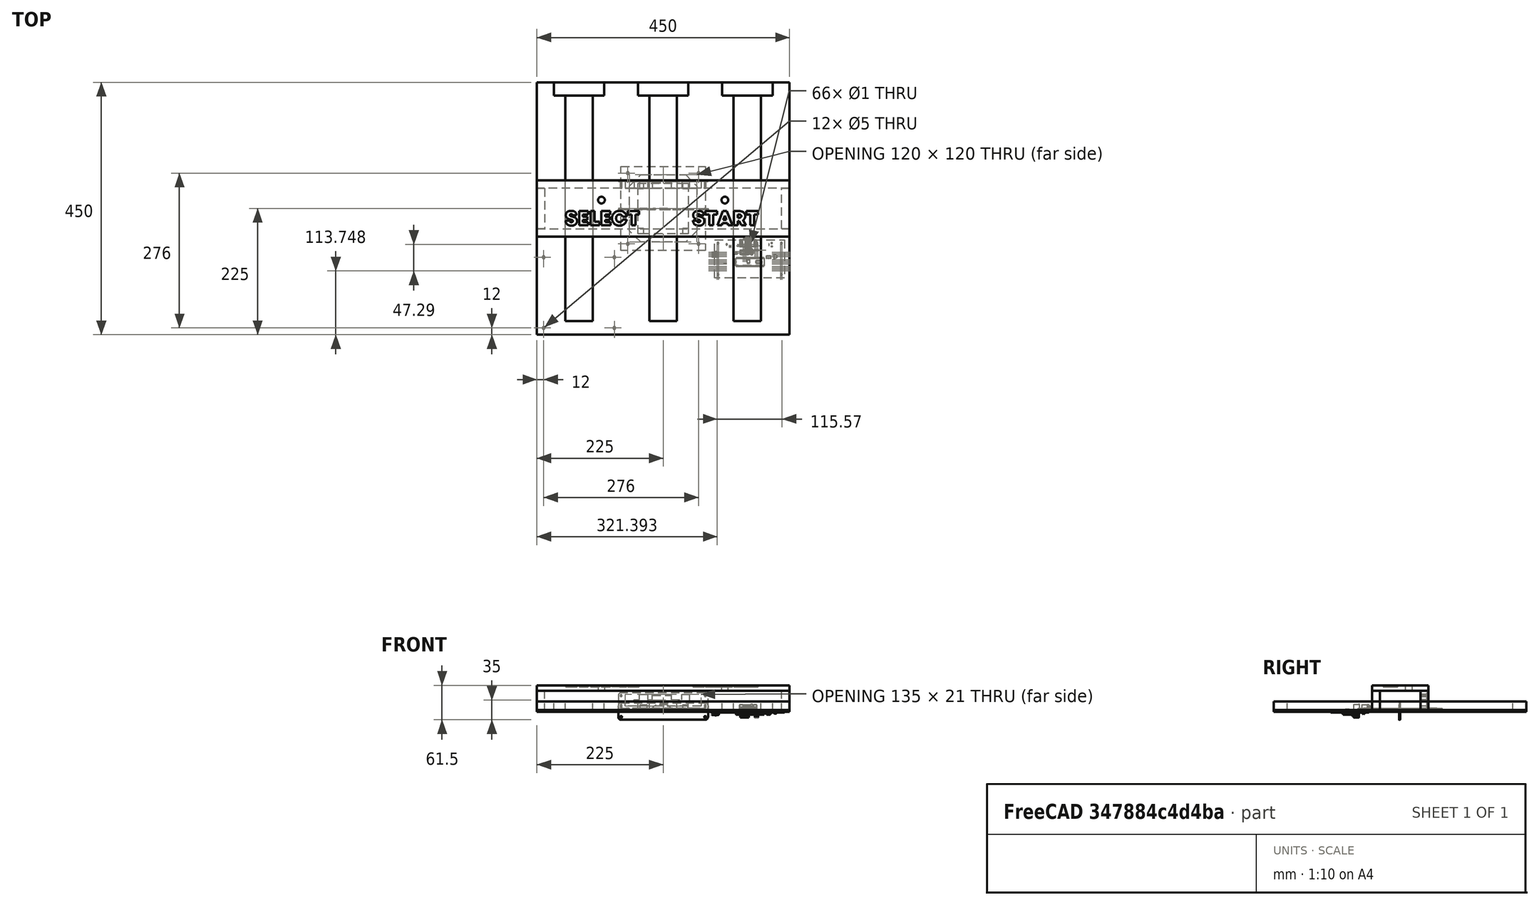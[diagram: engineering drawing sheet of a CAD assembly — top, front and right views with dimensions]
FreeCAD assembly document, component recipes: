
FREECAD ASSEMBLY — COMPONENT RECIPES ("LittleDancePad")

This assembly document has 13 components, labeled P0..P12 below (a component is one placed body or linked part). 12 of them carry a construction recipe — the FreeCAD feature program that regenerates the part from scratch, quoted from this document or its linked companion documents; the rest are supplied as boundary geometry only. No exploded tour is included for this assembly.
COMPONENT P0 — geometry summary ("PCB"; no construction recipe available for this part):
  bounding box: 135.6 x 74.1 x 23.8 mm
  tessellated surface: 47,226 triangles
  volume: 23545 mm^3 (10% of its bounding box)
COMPONENT P1 — recipe-attached ("Pad_BottomRight_Part", modeled in this document).
Construction recipe (the document's own serialized feature program — sketch geometry with constraints, then the solid features built on it; lengths are millimeters unless a unit is written):

FEATURE [Sketcher::SketchObject] Sketch001
  ArcFitTolerance = 0
  AttachmentSupport = -> [XY_Plane001]
  ExternalTypes = [0]
  FullyConstrained = true
  MakeInternals = false
  MapMode = 5
  _ExternalGeoVersion = 0
  sketch-geometry (4):
    g0: LineSegment StartX=-75 StartY=75 StartZ=0 EndX=75 EndY=75 EndZ=0
    g1: LineSegment StartX=75 StartY=75 StartZ=0 EndX=75 EndY=-75 EndZ=0
    g2: LineSegment StartX=75 StartY=-75 StartZ=0 EndX=-75 EndY=-75 EndZ=0
    g3: LineSegment StartX=-75 StartY=-75 StartZ=0 EndX=-75 EndY=75 EndZ=0
  constraints (11):
    c: Coincident(g0,g1)
    c: Coincident(g1,g2)
    c: Coincident(g2,g3)
    c: Coincident(g3,g0)
    c: Horizontal(g0)
    c: Horizontal(g2)
    c: Vertical(g1)
    c: Vertical(g3)
    c: Symmetric(g0,g1,g-1)
    c: DistanceX(g0,g0) = 150
    c: DistanceY(g1,g1) = 150
FEATURE [PartDesign::Pad] Pad001
  Direction = (0,0,1)
  Length = 6
  Length2 = 100
  Profile = -> Sketch001
  SideType = 0
  Suppressed = false
  Type = 0
  Type2 = 0
FEATURE [PartDesign::SubShapeBinder] Import  label="Import(*Sketch_Screw_Holes)"
  BindCopyOnChange = 0
  BindMode = 0
  ClaimChildren = false
  Context = -> Part [Body001.Import.]
  Fuse = false
  MakeFace = false
  OffsetFill = false
  OffsetIntersection = false
  OffsetJoinType = 0
  OffsetOpenResult = false
  PartialLoad = false
  Relative = true
  Support = -> [Link007]
  _Version = 8
FEATURE [PartDesign::Pocket] Pocket002
  BaseFeature = -> Pad001
  Direction = (0,0,-1)
  Length = 5
  Length2 = 100
  Profile = -> Import
  SideType = 2
  Suppressed = false
  Type = 1
  Type2 = 0
FEATURE [PartDesign::Body] Body001
  AllowCompound = true
  Group = -> [Sketch001,Pad001,Import,Pocket002]
  Origin = -> Origin006
  Tip = -> Pocket002
COMPONENT P2 — same part as P1; its construction recipe is shown at P1.
COMPONENT P3 — same part as P1; its construction recipe is shown at P1.
COMPONENT P4 — same part as P1; its construction recipe is shown at P1.
COMPONENT P5 — recipe-attached ("Pad_MiddleLeft_Part", modeled in this document).
Construction recipe (the document's own serialized feature program — sketch geometry with constraints, then the solid features built on it; lengths are millimeters unless a unit is written):

FEATURE [Sketcher::SketchObject] Sketch002
  ArcFitTolerance = 0
  AttachmentSupport = -> [XY_Plane002]
  ExternalTypes = [0]
  FullyConstrained = true
  MakeInternals = false
  MapMode = 5
  _ExternalGeoVersion = 0
  expr: Constraints[10] = <<Variables>>.PadLength
  expr: Constraints[9] = <<Variables>>.PadLength
  sketch-geometry (4):
    g0: LineSegment StartX=-75 StartY=75 StartZ=0 EndX=75 EndY=75 EndZ=0
    g1: LineSegment StartX=75 StartY=75 StartZ=0 EndX=75 EndY=-75 EndZ=0
    g2: LineSegment StartX=75 StartY=-75 StartZ=0 EndX=-75 EndY=-75 EndZ=0
    g3: LineSegment StartX=-75 StartY=-75 StartZ=0 EndX=-75 EndY=75 EndZ=0
  constraints (11):
    c: Coincident(g0,g1)
    c: Coincident(g1,g2)
    c: Coincident(g2,g3)
    c: Coincident(g3,g0)
    c: Horizontal(g0)
    c: Horizontal(g2)
    c: Vertical(g1)
    c: Vertical(g3)
    c: Symmetric(g0,g1,g-1)
    c: DistanceX(g0,g0) = 150
    c: DistanceY(g1,g1) = 150
FEATURE [PartDesign::Pad] Pad002
  Direction = (0,0,1)
  Length = 6
  Length2 = 100
  Profile = -> Sketch002
  SideType = 0
  Suppressed = false
  Type = 0
  Type2 = 0
  expr: Length = <<Variables>>.PadThickness
FEATURE [Sketcher::SketchObject] Sketch003
  ArcFitTolerance = 0
  AttachmentSupport = -> [XY_Plane002]
  ExternalGeometry = -> [Pad002]
  ExternalTypes = [0]
  FullyConstrained = true
  MakeInternals = false
  MapMode = 5
  _ExternalGeoVersion = 0
  expr: Constraints[10] = <<Variables>>.InnerPadBorderLength
  expr: Constraints[11] = <<Variables>>.InnerPadCornerLength
  expr: Constraints[12] = <<Variables>>.InnerPadBorderLength
  expr: Constraints[8] = <<Variables>>.InnerPadCornerLength
  sketch-geometry (8):
    g0: LineSegment StartX=-60 StartY=40 StartZ=0 EndX=-40 EndY=60 EndZ=0
    g1: LineSegment StartX=-40 StartY=60 StartZ=0 EndX=40 EndY=60 EndZ=0
    g2: LineSegment StartX=40 StartY=60 StartZ=0 EndX=60 EndY=40 EndZ=0
    g3: LineSegment StartX=60 StartY=40 StartZ=0 EndX=60 EndY=-40 EndZ=0
    g4: LineSegment StartX=60 StartY=-40 StartZ=0 EndX=40 EndY=-60 EndZ=0
    g5: LineSegment StartX=40 StartY=-60 StartZ=0 EndX=-40 EndY=-60 EndZ=0
    g6: LineSegment StartX=-40 StartY=-60 StartZ=0 EndX=-60 EndY=-40 EndZ=0
    g7: LineSegment StartX=-60 StartY=-40 StartZ=0 EndX=-60 EndY=40 EndZ=0
  constraints (18):
    c: Coincident(g0,g1)
    c: Coincident(g1,g2)
    c: Coincident(g2,g3)
    c: Coincident(g3,g4)
    c: Coincident(g4,g5)
    c: Coincident(g5,g6)
    c: Coincident(g6,g7)
    c: Coincident(g7,g0)
    c: DistanceX(g-3,g0) = 35
    c: Symmetric(g0,g1,g-2)
    c: DistanceY(g0,g-3) = 15
    c: DistanceY(g0,g-3) = 35
    c: DistanceX(g-3,g0) = 15
    c: Symmetric(g0,g6,g-1)
    c: Symmetric(g0,g5,g-1)
    c: Symmetric(g0,g2,g-2)
    c: Symmetric(g2,g3,g-1)
    c: Symmetric(g1,g4,g-1)
FEATURE [PartDesign::Pocket] Pocket
  BaseFeature = -> Pad002
  Direction = (0,0,-1)
  Length = 5
  Length2 = 100
  Profile = -> Sketch003
  SideType = 2
  Suppressed = false
  Type = 1
  Type2 = 0
FEATURE [Sketcher::SketchObject] Sketch004  label="Sketch_Screw_Holes"
  ArcFitTolerance = 0
  AttachmentSupport = -> [Pad002]
  ExternalGeometry = -> [Pad002]
  ExternalTypes = [0]
  FullyConstrained = true
  MakeInternals = false
  MapMode = 5
  Placement = pos=(0,0,0) rot=(1,0,0;3.14159rad)
  _ExternalGeoVersion = 0
  expr: Constraints[0] = <<Variables>>.ScrewCornerPosition
  expr: Constraints[1] = <<Variables>>.ScrewCornerPosition
  expr: Constraints[2] = <<Variables>>.PadScrewDiameter
  expr: Constraints[6] = <<Variables>>.PadScrewDiameter
  expr: Constraints[7] = <<Variables>>.PadScrewDiameter
  expr: Constraints[8] = <<Variables>>.PadScrewDiameter
  sketch-geometry (4):
    g0: Circle CenterX=-63 CenterY=63 CenterZ=0 NormalX=0 NormalY=0 NormalZ=1 AngleXU=0 Radius=2.5
    g1: Circle CenterX=63 CenterY=63 CenterZ=0 NormalX=0 NormalY=0 NormalZ=1 AngleXU=0 Radius=2.5
    g2: Circle CenterX=63 CenterY=-63 CenterZ=0 NormalX=0 NormalY=0 NormalZ=1 AngleXU=0 Radius=2.5
    g3: Circle CenterX=-63 CenterY=-63 CenterZ=0 NormalX=0 NormalY=0 NormalZ=1 AngleXU=0 Radius=2.5
  constraints (9):
    c: DistanceX(g-3,g0) = 12
    c: DistanceY(g0,g-3) = 12
    c: Diameter(g0) = 5
    c: Symmetric(g0,g1,g-2)
    c: Symmetric(g0,g3,g-1)
    c: Symmetric(g1,g2,g-1)
    c: Diameter(g1) = 5
    c: Diameter(g2) = 5
    c: Diameter(g3) = 5
FEATURE [PartDesign::Pocket] Pocket001  label="Screw_Pocket"
  BaseFeature = -> Pocket
  Direction = (0,0,1)
  Length = 5
  Length2 = 100
  Profile = -> Sketch004
  SideType = 2
  Suppressed = false
  Type = 1
  Type2 = 0
FEATURE [PartDesign::Body] Body002  label="Border_Body"
  AllowCompound = true
  Group = -> [Sketch002,Pad002,Sketch003,Sketch004,Pocket,Pocket001]
  Origin = -> Origin008
  Tip = -> Pocket001
FEATURE [Sketcher::SketchObject] Sketch005
  ArcFitTolerance = 0
  AttachmentSupport = -> [XY_Plane003]
  ExternalTypes = [0]
  FullyConstrained = true
  MakeInternals = false
  MapMode = 5
  _ExternalGeoVersion = 0
  expr: Constraints[9] = <<Variables>>.ContactLength
  sketch-geometry (4):
    g0: LineSegment StartX=-45 StartY=45 StartZ=0 EndX=45 EndY=45 EndZ=0
    g1: LineSegment StartX=45 StartY=45 StartZ=0 EndX=45 EndY=-45 EndZ=0
    g2: LineSegment StartX=45 StartY=-45 StartZ=0 EndX=-45 EndY=-45 EndZ=0
    g3: LineSegment StartX=-45 StartY=-45 StartZ=0 EndX=-45 EndY=45 EndZ=0
  constraints (11):
    c: Coincident(g0,g1)
    c: Coincident(g1,g2)
    c: Coincident(g2,g3)
    c: Coincident(g3,g0)
    c: Horizontal(g0)
    c: Horizontal(g2)
    c: Vertical(g1)
    c: Vertical(g3)
    c: Symmetric(g0,g1,g-1)
    c: DistanceX(g0,g0) = 90
    c: Equal(g0,g1)
FEATURE [PartDesign::Pad] Pad003
  Direction = (0,0,1)
  Length = 4
  Length2 = 100
  Profile = -> Sketch005
  SideType = 0
  Suppressed = false
  Type = 0
  Type2 = 0
FEATURE [PartDesign::Body] Body003  label="ContactBase_Body"
  AllowCompound = true
  Group = -> [Sketch005,Pad003]
  Origin = -> Origin010
  Tip = -> Pad003
COMPONENT P6 — same part as P5; its construction recipe is shown at P5.
COMPONENT P7 — same part as P5; its construction recipe is shown at P5.
COMPONENT P8 — recipe-attached ("Body_Part", modeled in this document).
Construction recipe (the document's own serialized feature program — sketch geometry with constraints, then the solid features built on it; lengths are millimeters unless a unit is written):

FEATURE [Sketcher::SketchObject] Sketch
  ArcFitTolerance = 0
  AttachmentSupport = -> [XY_Plane]
  ExternalTypes = [0]
  FullyConstrained = true
  MakeInternals = false
  MapMode = 5
  _ExternalGeoVersion = 0
  expr: Constraints[10] = <<Variables>>.OveralPadLength
  expr: Constraints[9] = <<Variables>>.OveralPadLength
  sketch-geometry (4):
    g0: LineSegment StartX=-225 StartY=225 StartZ=0 EndX=225 EndY=225 EndZ=0
    g1: LineSegment StartX=225 StartY=225 StartZ=0 EndX=225 EndY=-225 EndZ=0
    g2: LineSegment StartX=225 StartY=-225 StartZ=0 EndX=-225 EndY=-225 EndZ=0
    g3: LineSegment StartX=-225 StartY=-225 StartZ=0 EndX=-225 EndY=225 EndZ=0
  constraints (11):
    c: Coincident(g0,g1)
    c: Coincident(g1,g2)
    c: Coincident(g2,g3)
    c: Coincident(g3,g0)
    c: Horizontal(g0)
    c: Horizontal(g2)
    c: Vertical(g1)
    c: Vertical(g3)
    c: Symmetric(g0,g1,g-1)
    c: DistanceX(g0,g0) = 450
    c: DistanceY(g1,g1) = 450
FEATURE [PartDesign::Pad] Pad
  Direction = (0,0,1)
  Length = 18
  Length2 = 100
  Profile = -> Sketch
  SideType = 0
  Suppressed = false
  Type = 0
  Type2 = 0
  expr: Length = <<Variables>>.OverallPadThickness
FEATURE [PartDesign::Body] Body
  AllowCompound = true
  Group = -> [Sketch,Pad]
  Origin = -> Origin
  Tip = -> Pad
COMPONENT P9 — recipe-attached ("PolycarbonatePad_Part", modeled in this document).
Construction recipe (the document's own serialized feature program — sketch geometry with constraints, then the solid features built on it; lengths are millimeters unless a unit is written):

FEATURE [PartDesign::SubShapeBinder] Import003  label="Import003(*Sketch001)"
  BindCopyOnChange = 0
  BindMode = 0
  ClaimChildren = false
  Context = -> Part004 [Body006.Import003.]
  Fuse = false
  MakeFace = false
  OffsetFill = false
  OffsetIntersection = false
  OffsetJoinType = 0
  OffsetOpenResult = false
  PartialLoad = false
  Relative = true
  Support = -> [Link010]
  _Version = 8
FEATURE [PartDesign::Pad] Pad006
  Direction = (0,0,1)
  Length = 3
  Length2 = 100
  Profile = -> Import003
  SideType = 0
  Suppressed = false
  Type = 0
  Type2 = 0
FEATURE [PartDesign::SubShapeBinder] Import004  label="Import004(*Sketch_Screw_Holes)"
  BindCopyOnChange = 0
  BindMode = 0
  ClaimChildren = false
  Context = -> Part004 [Body006.Import004.]
  Fuse = false
  MakeFace = false
  OffsetFill = false
  OffsetIntersection = false
  OffsetJoinType = 0
  OffsetOpenResult = false
  PartialLoad = false
  Relative = true
  Support = -> [Link011]
  _Version = 8
FEATURE [PartDesign::Pocket] Pocket003
  BaseFeature = -> Pad006
  Direction = (0,0,-1)
  Length = 5
  Length2 = 100
  Profile = -> Import004
  SideType = 2
  Suppressed = false
  Type = 1
  Type2 = 0
FEATURE [PartDesign::LinearPattern] LinearPattern
  Direction = -> X_Axis007
  Length = 300
  Length2 = 100
  Mode = 0
  Mode2 = 0
  Occurrences = 3
  Occurrences2 = 1
  Offset = 150
  Offset2 = 10
  Reversed2 = false
  SpacingPattern = [0]
  SpacingPattern2 = [0]
  Spacings = [-1,-1]
  Suppressed = false
  TransformMode = 0
FEATURE [PartDesign::LinearPattern] LinearPattern001
  Direction = -> Y_Axis007
  Length = 300
  Length2 = 100
  Mode = 0
  Mode2 = 0
  Occurrences = 3
  Occurrences2 = 1
  Offset = 150
  Offset2 = 10
  Reversed2 = false
  SpacingPattern = [0]
  SpacingPattern2 = [0]
  Spacings = [-1,-1]
  Suppressed = false
  TransformMode = 0
FEATURE [PartDesign::MultiTransform] MultiTransform
  BaseFeature = -> Pocket003
  Originals = -> [Pocket003,Pad006]
  Suppressed = false
  TransformMode = 0
  Transformations = -> [LinearPattern,LinearPattern001]
FEATURE [PartDesign::Body] Body006
  AllowCompound = true
  Group = -> [Import003,Pad006,Import004,Pocket003,MultiTransform,LinearPattern,LinearPattern001]
  Origin = -> Origin014
  Tip = -> MultiTransform
COMPONENT P10 — recipe-attached ("Box_Part", modeled in this document).
Construction recipe (the document's own serialized feature program — sketch geometry with constraints, then the solid features built on it; lengths are millimeters unless a unit is written):

FEATURE [Sketcher::SketchObject] Sketch007
  ArcFitTolerance = 0
  AttachmentSupport = -> [XY_Plane008]
  ExternalTypes = [0]
  FullyConstrained = true
  MakeInternals = false
  MapMode = 5
  _ExternalGeoVersion = 0
  expr: Constraints[11] = <<Variables>>.OveralPadLength / 2
  expr: Constraints[8] = <<Variables>>.OveralPadLength
  sketch-geometry (4):
    g0: LineSegment StartX=-225 StartY=-36 StartZ=0 EndX=225 EndY=-36 EndZ=0
    g1: LineSegment StartX=225 StartY=-36 StartZ=0 EndX=225 EndY=-50 EndZ=0
    g2: LineSegment StartX=225 StartY=-50 StartZ=0 EndX=-225 EndY=-50 EndZ=0
    g3: LineSegment StartX=-225 StartY=-50 StartZ=0 EndX=-225 EndY=-36 EndZ=0
  constraints (12):
    c: Coincident(g0,g1)
    c: Coincident(g1,g2)
    c: Coincident(g2,g3)
    c: Coincident(g3,g0)
    c: Horizontal(g0)
    c: Horizontal(g2)
    c: Vertical(g1)
    c: Vertical(g3)
    c: DistanceX(g0,g0) = 450
    c: DistanceY(g3,g3) = 14
    c: DistanceY(g1,g-1) = 50
    c: DistanceX(g-1,g0) = 225
FEATURE [PartDesign::Pad] Pad007
  Direction = (0,0,1)
  Length = 37
  Length2 = 100
  Profile = -> Sketch007
  SideType = 0
  Suppressed = false
  Type = 0
  Type2 = 0
FEATURE [PartDesign::Body] Body007
  AllowCompound = true
  Group = -> [Sketch007,Pad007]
  Origin = -> Origin016
  Tip = -> Pad007
FEATURE [Sketcher::SketchObject] Sketch008
  ArcFitTolerance = 0
  AttachmentSupport = -> [XY_Plane009]
  ExternalTypes = [0]
  FullyConstrained = true
  MakeInternals = false
  MapMode = 5
  _ExternalGeoVersion = 0
  expr: Constraints[11] = <<Variables>>.OveralPadLength / 2
  expr: Constraints[8] = <<Variables>>.OveralPadLength
  sketch-geometry (4):
    g0: LineSegment StartX=-225 StartY=50 StartZ=0 EndX=225 EndY=50 EndZ=0
    g1: LineSegment StartX=225 StartY=50 StartZ=0 EndX=225 EndY=36 EndZ=0
    g2: LineSegment StartX=225 StartY=36 StartZ=0 EndX=-225 EndY=36 EndZ=0
    g3: LineSegment StartX=-225 StartY=36 StartZ=0 EndX=-225 EndY=50 EndZ=0
  constraints (12):
    c: Coincident(g0,g1)
    c: Coincident(g1,g2)
    c: Coincident(g2,g3)
    c: Coincident(g3,g0)
    c: Horizontal(g0)
    c: Horizontal(g2)
    c: Vertical(g1)
    c: Vertical(g3)
    c: DistanceX(g0,g0) = 450
    c: DistanceY(g1,g1) = 14
    c: DistanceY(g-1,g0) = 50
    c: DistanceX(g-1,g0) = 225
FEATURE [PartDesign::Pad] Pad008
  Direction = (0,0,1)
  Length = 37
  Length2 = 100
  Profile = -> Sketch008
  SideType = 0
  Suppressed = false
  Type = 0
  Type2 = 0
FEATURE [Sketcher::SketchObject] Sketch009
  ArcFitTolerance = 0
  AttachmentSupport = -> [XY_Plane010]
  ExternalTypes = [0]
  FullyConstrained = false
  MakeInternals = false
  MapMode = 5
  _ExternalGeoVersion = 0
  sketch-geometry (4):
    g0: LineSegment StartX=-225 StartY=36 StartZ=0 EndX=-211 EndY=36 EndZ=0
    g1: LineSegment StartX=-211 StartY=36 StartZ=0 EndX=-211 EndY=-36 EndZ=0
    g2: LineSegment StartX=-211 StartY=-36 StartZ=0 EndX=-225 EndY=-36 EndZ=0
    g3: LineSegment StartX=-225 StartY=-36 StartZ=0 EndX=-225 EndY=36 EndZ=0
  constraints (9):
    c: Coincident(g0,g1)
    c: Coincident(g1,g2)
    c: Coincident(g2,g3)
    c: Coincident(g3,g0)
    c: Horizontal(g0)
    c: Vertical(g1)
    c: Coincident(g0,g-3)
    c: Coincident(g2,g-4)
    c: DistanceX(g0,g0) = 14
FEATURE [PartDesign::Pad] Pad009
  Direction = (0,0,1)
  Length = 37
  Length2 = 100
  Profile = -> Sketch009
  SideType = 0
  Suppressed = false
  Type = 0
  Type2 = 0
FEATURE [PartDesign::Body] Body009
  AllowCompound = true
  Group = -> [Sketch009,Pad009]
  Origin = -> Origin018
  Tip = -> Pad009
FEATURE [Sketcher::SketchObject] Sketch010
  ArcFitTolerance = 0
  AttachmentSupport = -> [XY_Plane011]
  ExternalTypes = [0]
  FullyConstrained = true
  MakeInternals = false
  MapMode = 5
  _ExternalGeoVersion = 0
  sketch-geometry (4):
    g0: LineSegment StartX=211 StartY=36 StartZ=0 EndX=225 EndY=36 EndZ=0
    g1: LineSegment StartX=225 StartY=36 StartZ=0 EndX=225 EndY=-36 EndZ=0
    g2: LineSegment StartX=225 StartY=-36 StartZ=0 EndX=211 EndY=-36 EndZ=0
    g3: LineSegment StartX=211 StartY=-36 StartZ=0 EndX=211 EndY=36 EndZ=0
  constraints (10):
    c: Coincident(g0,g1)
    c: Coincident(g1,g2)
    c: Coincident(g2,g3)
    c: Coincident(g3,g0)
    c: Horizontal(g2)
    c: Vertical(g3)
    c: Coincident(g-3,g0)
    c: Coincident(g1,g-4)
    c: DistanceX(g0,g0) = 14
    c: Horizontal(g0)
FEATURE [PartDesign::Pad] Pad010
  Direction = (0,0,1)
  Length = 37
  Length2 = 100
  Profile = -> Sketch010
  SideType = 0
  Suppressed = false
  Type = 0
  Type2 = 0
FEATURE [PartDesign::Body] Body010
  AllowCompound = true
  Group = -> [Sketch010,Pad010]
  Origin = -> Origin019
  Tip = -> Pad010
FEATURE [Sketcher::SketchObject] Sketch011
  ArcFitTolerance = 0
  AttachmentSupport = -> [XY_Plane012]
  ExternalTypes = [0]
  FullyConstrained = true
  MakeInternals = false
  MapMode = 5
  _ExternalGeoVersion = 0
  sketch-geometry (4):
    g0: LineSegment StartX=-225 StartY=50 StartZ=0 EndX=225 EndY=50 EndZ=0
    g1: LineSegment StartX=225 StartY=50 StartZ=0 EndX=225 EndY=-50 EndZ=0
    g2: LineSegment StartX=225 StartY=-50 StartZ=0 EndX=-225 EndY=-50 EndZ=0
    g3: LineSegment StartX=-225 StartY=-50 StartZ=0 EndX=-225 EndY=50 EndZ=0
  constraints (9):
    c: Coincident(g0,g1)
    c: Coincident(g1,g2)
    c: Coincident(g2,g3)
    c: Coincident(g3,g0)
    c: Horizontal(g0)
    c: Vertical(g3)
    c: Coincident(g0,g-5)
    c: Coincident(g-6,g1)
    c: Coincident(g2,g-4)
FEATURE [PartDesign::Pad] Pad011
  Direction = (0,0,1)
  Length = 10
  Length2 = 100
  Profile = -> Sketch011
  SideType = 0
  Suppressed = false
  Type = 0
  Type2 = 0
FEATURE [Sketcher::SketchObject] Sketch012
  ArcFitTolerance = 0
  AttachmentSupport = -> [XY_Plane012]
  ExternalGeometry = -> [Pad011]
  ExternalTypes = [0]
  FullyConstrained = true
  MakeInternals = false
  MapMode = 5
  _ExternalGeoVersion = 0
  sketch-geometry (2):
    g0: Circle CenterX=110 CenterY=15 CenterZ=0 NormalX=0 NormalY=0 NormalZ=1 AngleXU=0 Radius=6
    g1: Circle CenterX=-110 CenterY=15 CenterZ=0 NormalX=0 NormalY=0 NormalZ=1 AngleXU=0 Radius=6
  constraints (5):
    c: Diameter(g0) = 12
    c: DistanceX(g-1,g0) = 110
    c: DistanceY(g0,g-3) = 35
    c: Diameter(g1) = 12
    c: Symmetric(g0,g1,g-2)
FEATURE [PartDesign::Pocket] Pocket004
  BaseFeature = -> Pad011
  Direction = (0,0,-1)
  Length = 5
  Length2 = 100
  Profile = -> Sketch012
  SideType = 2
  Suppressed = false
  Type = 1
  Type2 = 0
FEATURE [PartDesign::SubShapeBinder] Import011  label="Import011(START_ShapeString)"
  BindCopyOnChange = 0
  BindMode = 0
  ClaimChildren = false
  Context = -> Part005 [Body011.Import011.]
  Fuse = false
  MakeFace = false
  OffsetFill = false
  OffsetIntersection = false
  OffsetJoinType = 0
  OffsetOpenResult = false
  PartialLoad = false
  Relative = true
  Support = -> [ShapeString]
  _Version = 8
FEATURE [PartDesign::Pocket] Pocket005  label="START_Pocket"
  BaseFeature = -> Pocket004
  Direction = (0,0,-1)
  Length = 3.1
  Length2 = 100
  Profile = -> Import011
  SideType = 0
  Suppressed = false
  Type = 0
  Type2 = 0
FEATURE [PartDesign::SubShapeBinder] Import012  label="Import012(SELECT_ShapeString)"
  BindCopyOnChange = 0
  BindMode = 0
  ClaimChildren = false
  Context = -> Part005 [Body011.Pocket006.Import012.]
  Fuse = false
  MakeFace = false
  OffsetFill = false
  OffsetIntersection = false
  OffsetJoinType = 0
  OffsetOpenResult = false
  PartialLoad = false
  Relative = true
  Support = -> [ShapeString001]
  _Version = 8
FEATURE [PartDesign::Pocket] Pocket006  label="SELECT_Pocket"
  BaseFeature = -> Pocket005
  Direction = (0,0,-1)
  Length = 3.1
  Length2 = 100
  Profile = -> Import012
  SideType = 0
  Suppressed = false
  Type = 0
  Type2 = 0
FEATURE [PartDesign::Body] Body011  label="Panel_Body"
  AllowCompound = true
  Group = -> [Sketch011,Pad011,Sketch012,Pocket004,Import011,Pocket005,Import012,Pocket006]
  Origin = -> Origin020
  Placement = pos=(0,0,37) rot=(0,0,1;0rad)
  Tip = -> Pocket006
FEATURE [Sketcher::SketchObject] Sketch015
  ArcFitTolerance = 0
  AttachmentSupport = -> [Pad008]
  ExternalTypes = [0]
  FullyConstrained = true
  MakeInternals = false
  MapMode = 5
  Placement = pos=(0,50,0) rot=(0,0.707107,0.707107;3.14159rad)
  _ExternalGeoVersion = 0
  sketch-geometry (22):
    g0: LineSegment StartX=-67.5 StartY=18 StartZ=0 EndX=-46.5 EndY=18 EndZ=0
    g1: LineSegment StartX=-46.5 StartY=18 StartZ=0 EndX=-46.5 EndY=31 EndZ=0
    g2: LineSegment StartX=-46.5 StartY=31 StartZ=0 EndX=-33.5 EndY=31 EndZ=0
    g3: LineSegment StartX=-33.5 StartY=31 StartZ=0 EndX=-33.5 EndY=21 EndZ=0
    g4: LineSegment StartX=-33.5 StartY=21 StartZ=0 EndX=-14.5 EndY=21 EndZ=0
    g5: LineSegment StartX=-14.5 StartY=21 StartZ=0 EndX=-14.5 EndY=29 EndZ=0
    g6: LineSegment StartX=-14.5 StartY=29 StartZ=0 EndX=19.5 EndY=29 EndZ=0
    g7: LineSegment StartX=19.5 StartY=29 StartZ=0 EndX=19.5 EndY=21 EndZ=0
    g8: LineSegment StartX=19.5 StartY=21 StartZ=0 EndX=27.5 EndY=21 EndZ=0
    g9: LineSegment StartX=27.5 StartY=21 StartZ=0 EndX=27.5 EndY=31 EndZ=0
    g10: LineSegment StartX=27.5 StartY=31 StartZ=0 EndX=42.5 EndY=31 EndZ=0
    g11: LineSegment StartX=42.5 StartY=31 StartZ=0 EndX=42.5 EndY=21 EndZ=0
    g12: LineSegment StartX=67.5 StartY=18 StartZ=0 EndX=67.5 EndY=10 EndZ=0
    g13: LineSegment StartX=67.5 StartY=10 StartZ=0 EndX=-67.5 EndY=10 EndZ=0
    g14: LineSegment StartX=-67.5 StartY=10 StartZ=0 EndX=-67.5 EndY=18 EndZ=0
    g15: LineSegment StartX=42.5 StartY=21 StartZ=0 EndX=51.5 EndY=21 EndZ=0
    g16: LineSegment StartX=51.5 StartY=21 StartZ=0 EndX=51.5 EndY=18 EndZ=0
    g17: LineSegment StartX=51.5 StartY=18 StartZ=0 EndX=67.5 EndY=18 EndZ=0
    g18: Circle CenterX=-75 CenterY=28.5 CenterZ=0 NormalX=0 NormalY=0 NormalZ=1 AngleXU=0 Radius=1.75
    g19: Circle CenterX=-75 CenterY=8.5 CenterZ=0 NormalX=0 NormalY=0 NormalZ=1 AngleXU=0 Radius=1.75
    g20: Circle CenterX=75 CenterY=28.5 CenterZ=0 NormalX=0 NormalY=0 NormalZ=1 AngleXU=0 Radius=1.75
    g21: Circle CenterX=75 CenterY=8.5 CenterZ=0 NormalX=0 NormalY=0 NormalZ=1 AngleXU=0 Radius=1.75
  constraints (65):
    c: Horizontal(g0)
    c: Coincident(g0,g1)
    c: Vertical(g1)
    c: Coincident(g1,g2)
    c: Horizontal(g2)
    c: Coincident(g2,g3)
    c: Vertical(g3)
    c: Coincident(g3,g4)
    c: Horizontal(g4)
    c: Vertical(g5)
    c: Coincident(g5,g6)
    c: Horizontal(g6)
    c: Coincident(g6,g7)
    c: Vertical(g7)
    c: Coincident(g7,g8)
    c: Horizontal(g8)
    c: Coincident(g8,g9)
    c: Coincident(g9,g10)
    c: Horizontal(g10)
    c: Coincident(g10,g11)
    c: Vertical(g12)
    c: Coincident(g12,g13)
    c: Coincident(g13,g14)
    c: Coincident(g14,g0)
    c: Vertical(g14)
    c: DistanceX(g13,g13) = 135
    c: Symmetric(g13,g12,g-2)
    c: DistanceY(g14,g14) = 8
    c: DistanceY(g12,g12) = 8
    c: DistanceY(g-1,g0) = 18
    c: DistanceX(g0,g0) = 21
    c: DistanceX(g2,g2) = 13
    c: DistanceY(g1,g1) = 13
    c: DistanceY(g3,g3) = 10
    c: DistanceY(g7,g7) = 8
    c: DistanceY(g9,g9) = 10
    c: DistanceY(g11,g11) = 10
    c: Vertical(g9)
    c: Vertical(g11)
    c: Coincident(g11,g15)
    c: Horizontal(g15)
    c: Coincident(g15,g16)
    c: Vertical(g16)
    c: Coincident(g16,g17)
    c: Coincident(g17,g12)
    c: Horizontal(g17)
    c: Coincident(g5,g4)
    c: DistanceY(g5,g5) = 8
    c: DistanceX(g4,g4) = 19
    c: DistanceX(g6,g6) = 34
    c: DistanceX(g8,g8) = 8
    c: DistanceX(g10,g10) = 15
    c: DistanceX(g17,g17) = 16
    c: Diameter(g18) = 3.5
    c: Diameter(g19) = 3.5
    c: Diameter(g20) = 3.5
    c: Diameter(g21) = 3.5
    c: DistanceY(g-1,g19) = 8.5
    c: DistanceY(g-1,g21) = 8.5
    c: DistanceY(g-1,g18) = 28.5
    c: DistanceY(g-1,g20) = 28.5
    c: DistanceX(g19,g-1) = 75
    c: DistanceX(g18,g-1) = 75
    c: DistanceX(g-1,g21) = 75
    c: DistanceX(g-1,g20) = 75
FEATURE [PartDesign::Pocket] Pocket007
  BaseFeature = -> Pad008
  Direction = (0,-1,2e-16)
  Length = 5
  Length2 = 100
  Profile = -> Sketch015
  SideType = 2
  Suppressed = false
  Type = 1
  Type2 = 0
FEATURE [Sketcher::SketchObject] Sketch016
  ArcFitTolerance = 0
  AttachmentSupport = -> [Pocket007]
  ExternalGeometry = -> [Pocket007]
  ExternalTypes = [0]
  FullyConstrained = true
  MakeInternals = false
  MapMode = 5
  Placement = pos=(0,50,0) rot=(0,0.707107,0.707107;3.14159rad)
  _ExternalGeoVersion = 0
  sketch-geometry (4):
    g0: LineSegment StartX=-14.5 StartY=31 StartZ=0 EndX=19.5 EndY=31 EndZ=0
    g1: LineSegment StartX=19.5 StartY=31 StartZ=0 EndX=19.5 EndY=29 EndZ=0
    g2: LineSegment StartX=19.5 StartY=29 StartZ=0 EndX=-14.5 EndY=29 EndZ=0
    g3: LineSegment StartX=-14.5 StartY=29 StartZ=0 EndX=-14.5 EndY=31 EndZ=0
  constraints (10):
    c: Coincident(g0,g1)
    c: Coincident(g1,g2)
    c: Coincident(g2,g3)
    c: Coincident(g3,g0)
    c: Horizontal(g0)
    c: Vertical(g1)
    c: Vertical(g3)
    c: Coincident(g2,g-3)
    c: Coincident(g1,g-3)
    c: DistanceY(g3,g3) = 2
FEATURE [PartDesign::Pocket] Pocket008
  BaseFeature = -> Pocket007
  Direction = (0,-1,2e-16)
  Length = 4.5
  Length2 = 100
  Profile = -> Sketch016
  SideType = 0
  Suppressed = false
  Type = 0
  Type2 = 0
FEATURE [Sketcher::SketchObject] Sketch019
  ArcFitTolerance = 0
  AttachmentSupport = -> [Pocket008]
  ExternalGeometry = -> [Pocket008]
  ExternalTypes = [0]
  FullyConstrained = true
  MakeInternals = false
  MapMode = 5
  Placement = pos=(0,50,0) rot=(0,0.707107,0.707107;3.14159rad)
  _ExternalGeoVersion = 0
  sketch-geometry (8):
    g0: ArcOfCircle CenterX=-75 CenterY=28.5 CenterZ=0 NormalX=0 NormalY=0 NormalZ=1 AngleXU=0 Radius=5 StartAngle=1.5708 EndAngle=3.14159
    g1: ArcOfCircle CenterX=-75 CenterY=8.5 CenterZ=0 NormalX=0 NormalY=0 NormalZ=1 AngleXU=0 Radius=5 StartAngle=3.14159 EndAngle=4.71239
    g2: ArcOfCircle CenterX=75 CenterY=28.5 CenterZ=0 NormalX=0 NormalY=0 NormalZ=1 AngleXU=0 Radius=5 StartAngle=4.5489e-06 EndAngle=1.5708
    g3: ArcOfCircle CenterX=75 CenterY=8.5 CenterZ=0 NormalX=0 NormalY=0 NormalZ=1 AngleXU=0 Radius=5 StartAngle=4.71239 EndAngle=6.28319
    g4: LineSegment StartX=-75 StartY=33.5 StartZ=0 EndX=75 EndY=33.5 EndZ=0
    g5: LineSegment StartX=80 StartY=28.5 StartZ=0 EndX=80 EndY=8.5 EndZ=0
    g6: LineSegment StartX=75 StartY=3.5 StartZ=0 EndX=-75 EndY=3.5 EndZ=0
    g7: LineSegment StartX=-80 StartY=8.5 StartZ=0 EndX=-80 EndY=28.5 EndZ=0
  constraints (26):
    c: Coincident(g4,g0)
    c: Coincident(g4,g2)
    c: Coincident(g5,g2)
    c: Coincident(g5,g3)
    c: Vertical(g5)
    c: Coincident(g6,g3)
    c: Coincident(g6,g1)
    c: Horizontal(g6)
    c: Coincident(g7,g1)
    c: Coincident(g7,g0)
    c: Vertical(g7)
    c: Radius(g0) = 5
    c: Radius(g1) = 5
    c: Radius(g2) = 5
    c: Radius(g3) = 5
    c: DistanceX(g1,g3) = 160
    c: DistanceY(g1,g0) = 30
    c: Symmetric(g0,g2,g-2)
    c: DistanceY(g-1,g1) = 3.5
    c: Symmetric(g1,g3,g-2)
    c: DistanceX(g1,g1) = 5
    c: DistanceX(g0,g0) = 5
    c: DistanceY(g0,g0) = 5
    c: DistanceY(g1,g1) = 5
    c: DistanceY(g3,g3) = 5
    c: DistanceX(g2,g2) = 5
FEATURE [PartDesign::Pocket] Pocket010
  BaseFeature = -> Pocket008
  Direction = (0,-1,2e-16)
  Length = 2
  Length2 = 100
  Profile = -> Sketch019
  SideType = 0
  Suppressed = false
  Type = 0
  Type2 = 0
FEATURE [PartDesign::Body] Body008
  AllowCompound = true
  Group = -> [Sketch008,Pad008,Sketch015,Pocket007,Sketch016,Pocket008,Sketch019,Pocket010]
  Origin = -> Origin017
  Tip = -> Pocket010
COMPONENT P11 — recipe-attached ("Bases_Part", modeled in this document).
Construction recipe (the document's own serialized feature program — sketch geometry with constraints, then the solid features built on it; lengths are millimeters unless a unit is written):

FEATURE [Sketcher::SketchObject] Sketch013
  ArcFitTolerance = 0
  AttachmentSupport = -> [XY_Plane013]
  ExternalTypes = [0]
  FullyConstrained = true
  MakeInternals = false
  MapMode = 5
  _ExternalGeoVersion = 0
  sketch-geometry (4):
    g0: LineSegment StartX=-45 StartY=12 StartZ=0 EndX=45 EndY=12 EndZ=0
    g1: LineSegment StartX=45 StartY=12 StartZ=0 EndX=45 EndY=-12 EndZ=0
    g2: LineSegment StartX=45 StartY=-12 StartZ=0 EndX=-45 EndY=-12 EndZ=0
    g3: LineSegment StartX=-45 StartY=-12 StartZ=0 EndX=-45 EndY=12 EndZ=0
  constraints (11):
    c: Coincident(g0,g1)
    c: Coincident(g1,g2)
    c: Coincident(g2,g3)
    c: Coincident(g3,g0)
    c: Horizontal(g0)
    c: Horizontal(g2)
    c: Vertical(g1)
    c: Vertical(g3)
    c: Symmetric(g0,g1,g-1)
    c: DistanceX(g0,g0) = 90
    c: DistanceY(g1,g1) = 24
FEATURE [PartDesign::Pad] Pad012
  AlongSketchNormal = false
  Direction = (0,0,1)
  Length = 18
  Length2 = 100
  Profile = -> Sketch013
  SideType = 0
  Suppressed = false
  Type = 0
  Type2 = 0
FEATURE [PartDesign::LinearPattern] LinearPattern002
  BaseFeature = -> Pad012
  Direction = -> Sketch013 [H_Axis]
  Length = 300
  Length2 = 100
  Mode = 0
  Mode2 = 0
  Occurrences = 3
  Occurrences2 = 1
  Offset = 150
  Offset2 = 10
  Originals = -> [Pad012]
  Reversed2 = false
  SpacingPattern = [0]
  SpacingPattern2 = [0]
  Spacings = [-1,-1]
  Suppressed = false
  TransformMode = 0
FEATURE [PartDesign::Body] Body012
  AllowCompound = true
  Group = -> [Sketch013,Pad012,LinearPattern002]
  Origin = -> Origin022
  Placement = pos=(-150,213,0) rot=(0,0,1;0rad)
  Tip = -> LinearPattern002
FEATURE [Sketcher::SketchObject] Sketch014
  ArcFitTolerance = 0
  AttachmentSupport = -> [XY_Plane014]
  ExternalTypes = [0]
  FullyConstrained = true
  MakeInternals = false
  MapMode = 5
  _ExternalGeoVersion = 0
  sketch-geometry (4):
    g0: LineSegment StartX=-24.5 StartY=201 StartZ=0 EndX=24.5 EndY=201 EndZ=0
    g1: LineSegment StartX=24.5 StartY=201 StartZ=0 EndX=24.5 EndY=-201 EndZ=0
    g2: LineSegment StartX=24.5 StartY=-201 StartZ=0 EndX=-24.5 EndY=-201 EndZ=0
    g3: LineSegment StartX=-24.5 StartY=-201 StartZ=0 EndX=-24.5 EndY=201 EndZ=0
  constraints (11):
    c: Coincident(g0,g1)
    c: Coincident(g1,g2)
    c: Coincident(g2,g3)
    c: Coincident(g3,g0)
    c: Horizontal(g2)
    c: Vertical(g1)
    c: Vertical(g3)
    c: DistanceX(g0,g0) = 49
    c: Symmetric(g0,g0,g-2)
    c: DistanceY(g0,g-3) = 0
    c: DistanceY(g-4,g1) = 0
FEATURE [PartDesign::Pad] Pad013
  AlongSketchNormal = false
  Direction = (0,0,1)
  Length = 18
  Length2 = 100
  Profile = -> Sketch014
  SideType = 0
  Suppressed = false
  Type = 0
  Type2 = 0
FEATURE [PartDesign::LinearPattern] LinearPattern003
  BaseFeature = -> Pad013
  Direction = -> Sketch014 [H_Axis]
  Length = 300
  Length2 = 100
  Mode = 0
  Mode2 = 0
  Occurrences = 3
  Occurrences2 = 1
  Offset = 150
  Offset2 = 10
  Originals = -> [Pad013]
  Reversed2 = false
  SpacingPattern = [0]
  SpacingPattern2 = [0]
  Spacings = [-1,-1]
  Suppressed = false
  TransformMode = 0
FEATURE [PartDesign::Body] Body013
  AllowCompound = true
  Group = -> [Sketch014,Pad013,LinearPattern003]
  Origin = -> Origin023
  Placement = pos=(-150,0,0) rot=(0,0,1;0rad)
  Tip = -> LinearPattern003
COMPONENT P12 — recipe-attached ("ProfileFront_Part", modeled in this document).
Construction recipe (the document's own serialized feature program — sketch geometry with constraints, then the solid features built on it; lengths are millimeters unless a unit is written):

FEATURE [Sketcher::SketchObject] Sketch017
  ArcFitTolerance = 0
  AttachmentSupport = -> [XZ_Plane015]
  ExternalTypes = [0]
  FullyConstrained = true
  MakeInternals = false
  MapMode = 5
  Placement = pos=(0,0,0) rot=(1,0,0;1.5708rad)
  _ExternalGeoVersion = 0
  sketch-geometry (4):
    g0: LineSegment StartX=-80 StartY=15.5 StartZ=0 EndX=80 EndY=15.5 EndZ=0
    g1: LineSegment StartX=80 StartY=15.5 StartZ=0 EndX=80 EndY=-14.5 EndZ=0
    g2: LineSegment StartX=80 StartY=-14.5 StartZ=0 EndX=-80 EndY=-14.5 EndZ=0
    g3: LineSegment StartX=-80 StartY=-14.5 StartZ=0 EndX=-80 EndY=15.5 EndZ=0
  constraints (12):
    c: Vertical(g1)
    c: Vertical(g3)
    c: DistanceY(g1,g1) = 30
    c: Coincident(g3,g0)
    c: Coincident(g3,g2)
    c: Coincident(g0,g1)
    c: Coincident(g2,g1)
    c: DistanceX(g2,g2) = 160
    c: Horizontal(g2)
    c: DistanceY(g-4,g-4) = 37
    c: DistanceY(g0,g-4) = 3.5
    c: Symmetric(g0,g0,g-2)
FEATURE [PartDesign::Pad] Pad014
  AlongSketchNormal = false
  Direction = (0,-1,2e-16)
  Length = 2
  Length2 = 100
  Placement = pos=(0,0,0) rot=(1,0,0;1.5708rad)
  Profile = -> Sketch017
  SideType = 0
  Suppressed = false
  Type = 0
  Type2 = 0
FEATURE [Sketcher::SketchObject] Sketch018
  ArcFitTolerance = 0
  AttachmentSupport = -> [Pad014]
  ExternalGeometry = -> [Pad014]
  ExternalTypes = [0]
  FullyConstrained = true
  MakeInternals = false
  MapMode = 5
  Placement = pos=(0,1e-16,0) rot=(-1,0,0;1.5708rad)
  _ExternalGeoVersion = 0
  sketch-geometry (24):
    g0: LineSegment StartX=8.085 StartY=-12.5 StartZ=0 EndX=-13.515 EndY=-12.5 EndZ=0
    g1: LineSegment StartX=-13.515 StartY=-12.5 StartZ=0 EndX=-13.515 EndY=-9.85 EndZ=0
    g2: LineSegment StartX=-13.515 StartY=-9.85 StartZ=0 EndX=-15.015 EndY=-9.85 EndZ=0
    g3: LineSegment StartX=8.085 StartY=-12.5 StartZ=0 EndX=8.085 EndY=-9.85 EndZ=0
    g4: LineSegment StartX=8.085 StartY=-9.85 StartZ=0 EndX=9.585 EndY=-9.85 EndZ=0
    g5: LineSegment StartX=9.585 StartY=-3.15 StartZ=0 EndX=8.085 EndY=-3.15 EndZ=0
    g6: LineSegment StartX=8.085 StartY=-3.15 StartZ=0 EndX=8.085 EndY=-0.5 EndZ=0
    g7: LineSegment StartX=8.085 StartY=-0.5 StartZ=0 EndX=-13.515 EndY=-0.5 EndZ=0
    g8: LineSegment StartX=-13.515 StartY=-0.5 StartZ=0 EndX=-13.515 EndY=-3.15 EndZ=0
    g9: LineSegment StartX=-13.515 StartY=-3.15 StartZ=0 EndX=-15.015 EndY=-3.15 EndZ=0
    g10: ArcOfCircle CenterX=-15.015 CenterY=-6.5 CenterZ=0 NormalX=0 NormalY=0 NormalZ=1 AngleXU=0 Radius=3.35 StartAngle=1.5708 EndAngle=4.71239
    g11: ArcOfCircle CenterX=9.585 CenterY=-6.5 CenterZ=0 NormalX=0 NormalY=0 NormalZ=1 AngleXU=0 Radius=3.35 StartAngle=4.71239 EndAngle=7.85398
    g12: LineSegment StartX=-28.415 StartY=-11.5 StartZ=0 EndX=-41.415 EndY=-11.5 EndZ=0
    g13: LineSegment StartX=-41.415 StartY=-11.5 StartZ=0 EndX=-41.415 EndY=0 EndZ=0
    g14: LineSegment StartX=-41.415 StartY=0 StartZ=0 EndX=-28.415 EndY=0 EndZ=0
    g15: LineSegment StartX=-28.415 StartY=0 StartZ=0 EndX=-28.415 EndY=-11.5 EndZ=0
    g16: LineSegment StartX=44.385 StartY=-12 StartZ=0 EndX=34.385 EndY=-12 EndZ=0
    g17: LineSegment StartX=34.385 StartY=-12 StartZ=0 EndX=34.385 EndY=0 EndZ=0
    g18: LineSegment StartX=34.385 StartY=0 StartZ=0 EndX=44.385 EndY=0 EndZ=0
    g19: LineSegment StartX=44.385 StartY=0 StartZ=0 EndX=44.385 EndY=-12 EndZ=0
    g20: Circle CenterX=-75 CenterY=9.5 CenterZ=0 NormalX=0 NormalY=0 NormalZ=1 AngleXU=0 Radius=1.75
    g21: Circle CenterX=-75 CenterY=-10.5 CenterZ=0 NormalX=0 NormalY=0 NormalZ=1 AngleXU=0 Radius=1.75
    g22: Circle CenterX=75 CenterY=9.5 CenterZ=0 NormalX=0 NormalY=0 NormalZ=1 AngleXU=0 Radius=1.75
    g23: Circle CenterX=75 CenterY=-10.5 CenterZ=0 NormalX=0 NormalY=0 NormalZ=1 AngleXU=0 Radius=1.75
  constraints (74):
    c: Horizontal(g0)
    c: Coincident(g0,g1)
    c: Vertical(g1)
    c: Coincident(g1,g2)
    c: Coincident(g0,g3)
    c: Coincident(g3,g4)
    c: Horizontal(g4)
    c: Horizontal(g5)
    c: Coincident(g5,g6)
    c: Coincident(g6,g7)
    c: Horizontal(g7)
    c: Coincident(g7,g8)
    c: Vertical(g8)
    c: Coincident(g8,g9)
    c: Horizontal(g9)
    c: Coincident(g10,g9)
    c: Coincident(g10,g2)
    c: Coincident(g11,g5)
    c: Coincident(g11,g4)
    c: Coincident(g12,g13)
    c: Coincident(g13,g14)
    c: Coincident(g14,g15)
    c: Coincident(g15,g12)
    c: Horizontal(g12)
    c: Horizontal(g14)
    c: Vertical(g13)
    c: Vertical(g15)
    c: PointOnObject(g13,g-1)
    c: Coincident(g16,g17)
    c: Coincident(g17,g18)
    c: Coincident(g18,g19)
    c: Coincident(g19,g16)
    c: Horizontal(g16)
    c: Horizontal(g18)
    c: Vertical(g17)
    c: Vertical(g19)
    c: DistanceY(g7,g-1) = 0.5
    c: DistanceY(g13,g13) = 11.5
    c: DistanceY(g19,g19) = 12
    c: DistanceY(g17,g-1) = 0
    c: DistanceX(g12,g12) = 13
    c: DistanceX(g16,g16) = 10
    c: Vertical(g3)
    c: Vertical(g6)
    c: Horizontal(g2)
    c: DistanceX(g12,g-3) = 10.4
    c: DistanceX(g-4,g16) = 21.8
    c: DistanceX(g11,g-4) = 3
    c: DistanceX(g-3,g10) = 3
    c: DistanceX(g-3,g2) = 3
    c: DistanceX(g-3,g9) = 3
    c: DistanceX(g4,g-4) = 3
    c: DistanceX(g5,g-4) = 3
    c: DistanceX(g-3,g0) = 4.5
    c: DistanceX(g0,g-4) = 4.5
    c: DistanceX(g5,g-4) = 4.5
    c: DistanceX(g-3,g8) = 4.5
    c: DistanceY(g10,g-1) = 6.5
    c: DistanceY(g11,g-1) = 6.5
    c: DistanceY(g3,g5) = 6.7
    c: DistanceY(g1,g8) = 6.7
    c: Diameter(g20) = 3.5
    c: Diameter(g21) = 3.5
    c: Diameter(g22) = 3.5
    c: Diameter(g23) = 3.5
    c: DistanceX(g-5,g20) = 5
    c: DistanceX(g-5,g21) = 5
    c: DistanceX(g22,g-6) = 5
    c: DistanceX(g23,g-6) = 5
    c: DistanceY(g20,g-5) = 5
    c: DistanceY(g-5,g21) = 5
    c: DistanceY(g22,g-6) = 5
    c: DistanceY(g-6,g23) = 5
    c: DistanceY(g-7,g0) = 0.5
FEATURE [PartDesign::Fillet] Fillet
  Base = -> Pad014 [Edge2,Edge5,Edge1,Edge8]
  BaseFeature = -> Pad014
  Placement = pos=(0,0,0) rot=(1,0,0;1.5708rad)
  Radius = 5
  SupportTransform = false
  Suppressed = false
  UseAllEdges = false
FEATURE [PartDesign::Pocket] Pocket009
  BaseFeature = -> Fillet
  Direction = (0,-1,-2e-16)
  Length = 5
  Length2 = 100
  Placement = pos=(0,0,0) rot=(1,0,0;1.5708rad)
  Profile = -> Sketch018
  SideType = 2
  Suppressed = false
  Type = 1
  Type2 = 0
FEATURE [PartDesign::Body] Body014
  AllowCompound = true
  Group = -> [Sketch017,Pad014,Fillet,Sketch018,Pocket009]
  Origin = -> Origin027
  Tip = -> Pocket009
PROVENANCE & LICENSES
A FreeCAD (.FCStd) document from a public repository crawl; recipes are the document's own serialized feature recipes (and, for linked parts, companion documents' recipes).
License: mit.
